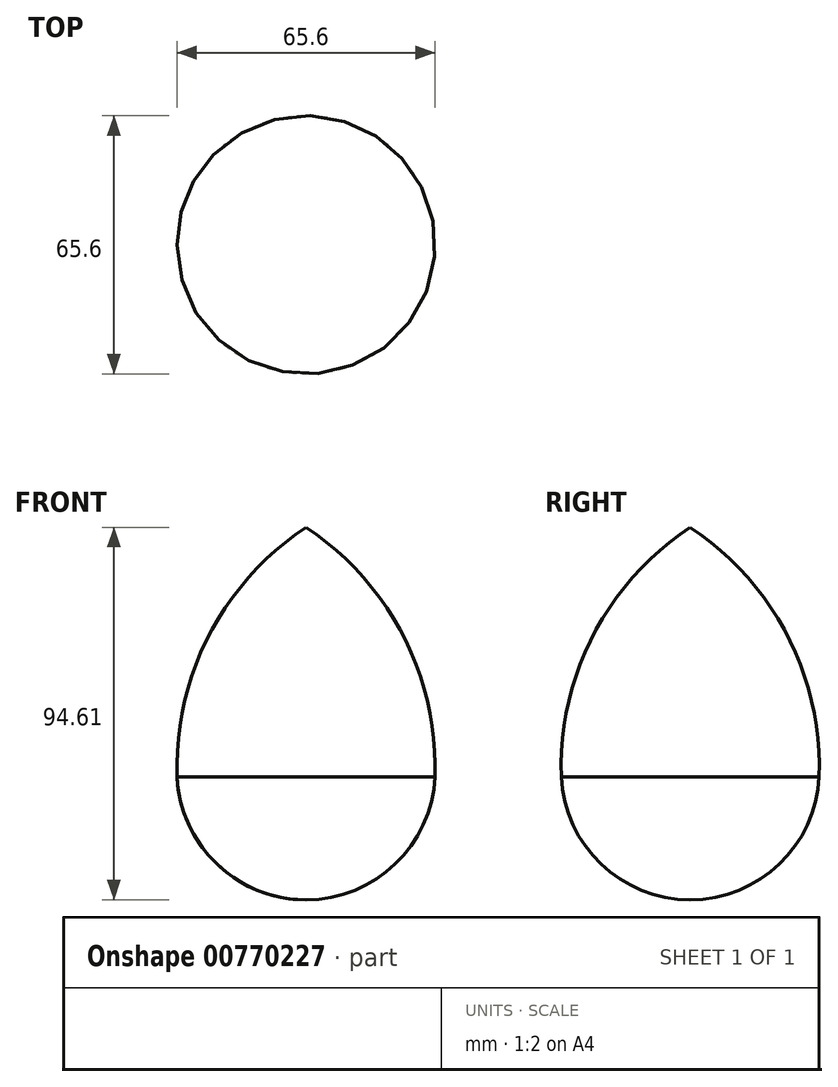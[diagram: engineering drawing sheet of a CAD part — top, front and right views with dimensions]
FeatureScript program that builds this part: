
annotation { "Feature Type Name" : "Feature", "Feature Type Description" : "" }
export const myFeature = defineFeature(function(context is Context, id is Id, definition is map)
    precondition{}
    {
        {
            var Q0;
            Q0=qCreatedBy(makeId("Front.planeOp"),FACE);
            var sketch = newSketch(context, id + "F0", { "sketchPlane" : qUnion([Q0])});
            skArc(sketch, "E0", {"start": v(-32.76, -22.6) * mm, "mid": v(-22.64, -44.8) * mm, "end": v(0, -53.87) * mm});
            skLineSegment(sketch, "E1", {"start": v(-32.76, -22.6) * mm, "end": v(0, 40.74) * mm});
            skArc(sketch, "E2", {"start": v(0, 40.74) * mm, "mid": v(-24.64, 13.34) * mm, "end": v(-32.76, -22.6) * mm});
            skLineSegment(sketch, "E3", {"start": v(0, 40.74) * mm, "end": v(0, -53.87) * mm});
            skSolve(sketch);
        }
        {
            var Q0;
            Q0=makeQuery(id+"F0.imprint","IMPRINT",FACE,{"disambiguationData":[TD([[makeQuery(id+"F0.imprint","IMPRINT",EDGE,{"derivedFrom":sQuery(id+"F0.wireOp",EDGE,"E0")}),1.0]])]});
            var Q1;
            Q1=makeQuery(id+"F0.imprint","IMPRINT",FACE,{"disambiguationData":[TD([[makeQuery(id+"F0.imprint","IMPRINT",EDGE,{"derivedFrom":sQuery(id+"F0.wireOp",EDGE,"E1")}),1.0]])]});
            var Q2;
            Q2=sQuery(id+"F0.wireOp",EDGE,"E3");
            revolve(context, id + "F1", {"surfaceOperationType" : NewSurfaceOperationType.NEW, "entities" : qUnion([Q0, Q1]), "axis" : qUnion([Q2]), "revolveType" : RevolveType.FULL});
        }
    });
